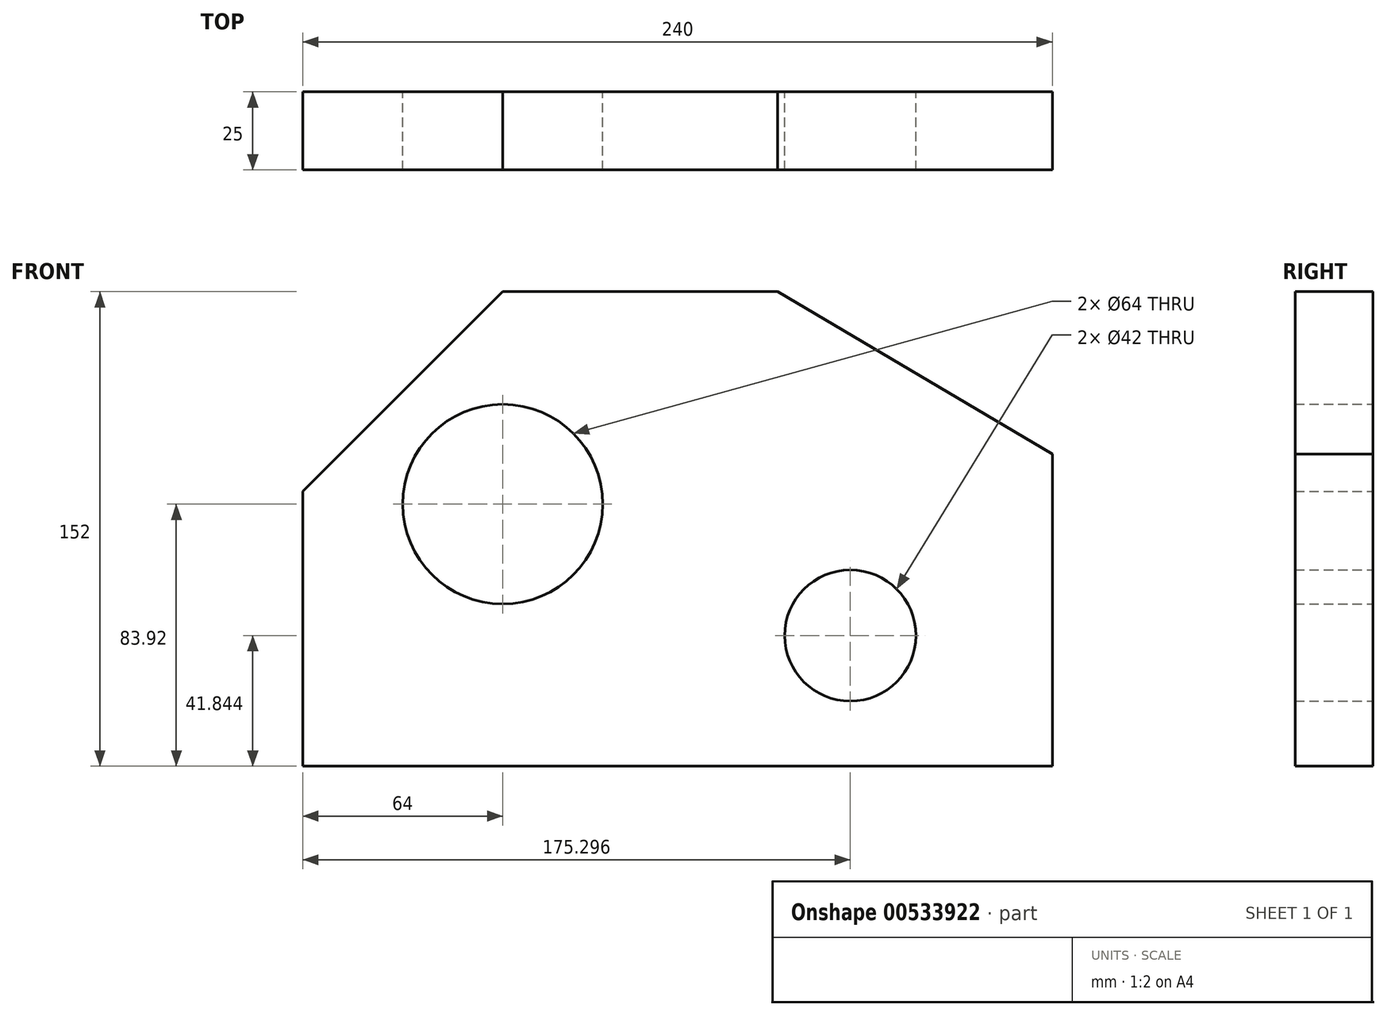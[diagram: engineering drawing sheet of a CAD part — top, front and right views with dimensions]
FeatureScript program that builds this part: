
annotation { "Feature Type Name" : "Feature", "Feature Type Description" : "" }
export const myFeature = defineFeature(function(context is Context, id is Id, definition is map)
    precondition{}
    {
        {
            var Q0;
            Q0=qCreatedBy(makeId("Front.planeOp"),FACE);
            var sketch = newSketch(context, id + "F0", { "sketchPlane" : qUnion([Q0])});
            skPoint(sketch, "E0.end.orphan", {"position": v(-133.56, 14.5) * mm});
            skPoint(sketch, "E1.start.orphan", {"position": v(119.9, 14.5) * mm});
            skLineSegment(sketch, "E2", {"start": v(-64, -83.92) * mm, "end": v(176, -83.92) * mm});
            skLineSegment(sketch, "E3", {"start": v(176, 16.08) * mm, "end": v(176, -83.92) * mm});
            skLineSegment(sketch, "E4", {"start": v(176, 16.08) * mm, "end": v(88, 68.08) * mm});
            skLineSegment(sketch, "E5", {"start": v(88, 68.08) * mm, "end": v(0, 68.08) * mm});
            skLineSegment(sketch, "E6", {"start": v(-64, -83.92) * mm, "end": v(-64, 4.08) * mm});
            skLineSegment(sketch, "E7", {"start": v(-64, 4.08) * mm, "end": v(0, 68.08) * mm});
            skCircle(sketch, "E8", {"center": v(0, 0) * mm, "radius": 32 * mm});
            skCircle(sketch, "E9", {"center": v(111.3, -42.08) * mm, "radius": 21 * mm});
            skSolve(sketch);
        }
        {
            var Q0;
            Q0=makeQuery(id+"F0.imprint","IMPRINT",FACE,{"disambiguationData":[TD([[makeQuery(id+"F0.imprint","IMPRINT",EDGE,{"derivedFrom":sQuery(id+"F0.wireOp",EDGE,"E2")}),1.0]])]});
            extrude(context, id + "F1", {"entities" : qUnion([Q0]), "depth" : 25 * mm, "offsetDistance" : 25 * mm});
        }
    });
